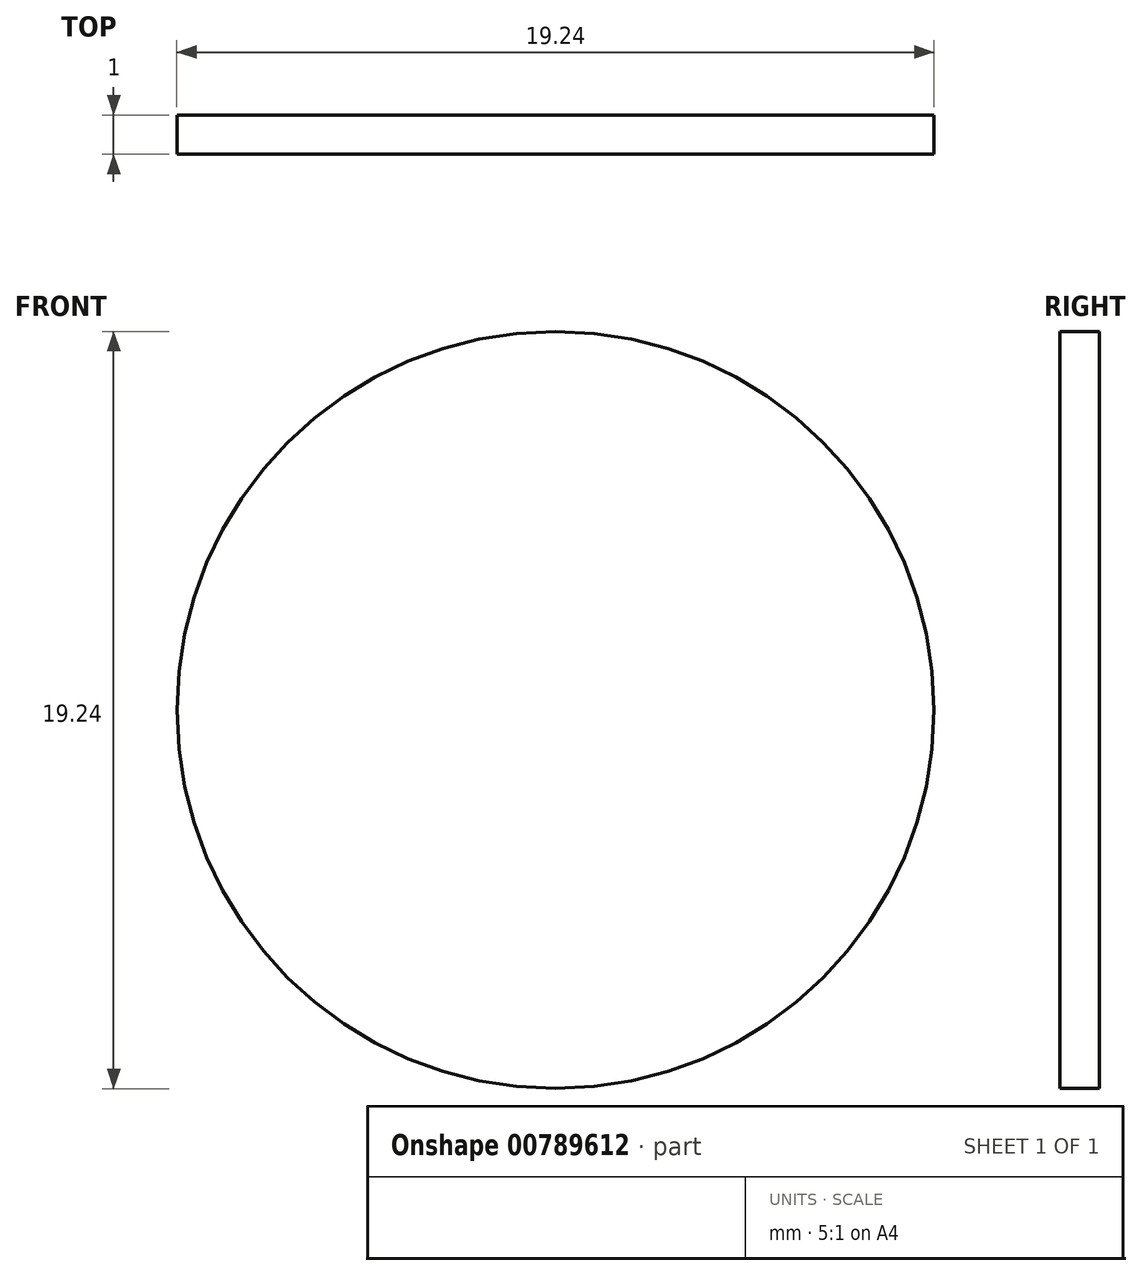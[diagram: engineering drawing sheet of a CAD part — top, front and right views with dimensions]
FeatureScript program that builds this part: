
annotation { "Feature Type Name" : "Feature", "Feature Type Description" : "" }
export const myFeature = defineFeature(function(context is Context, id is Id, definition is map)
    precondition{}
    {
        {
            var Q0;
            Q0=qCreatedBy(makeId("Front.planeOp"),FACE);
            var sketch = newSketch(context, id + "F0", { "sketchPlane" : qUnion([Q0])});
            skCircle(sketch, "E0", {"center": v(0, 0) * mm, "radius": 9.62 * mm});
            skSolve(sketch);
        }
        {
            var Q0;
            Q0 = qSketchRegion(id + "F0", true);
            extrude(context, id + "F1", {"entities" : qUnion([Q0]), "depth" : 1 * mm, "offsetDistance" : 25 * mm});
        }
    });
